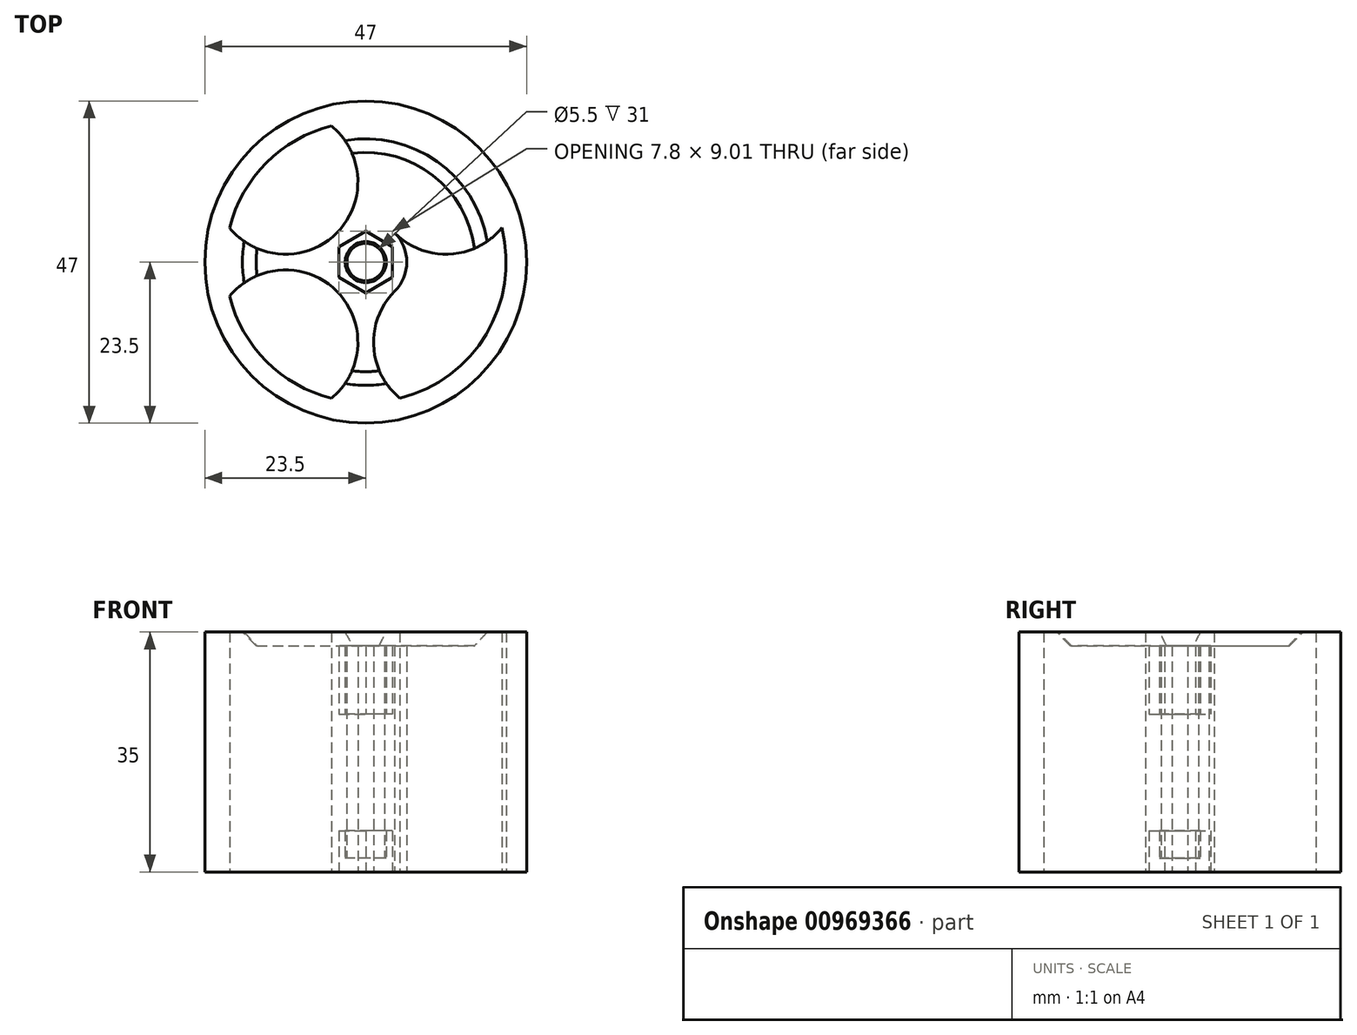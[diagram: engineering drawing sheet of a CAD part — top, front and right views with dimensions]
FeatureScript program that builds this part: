
annotation { "Feature Type Name" : "Feature", "Feature Type Description" : "" }
export const myFeature = defineFeature(function(context is Context, id is Id, definition is map)
    precondition{}
    {
        {
            var Q0;
            Q0=qCreatedBy(makeId("Top.planeOp"),FACE);
            var sketch = newSketch(context, id + "F0", { "sketchPlane" : qUnion([Q0])});
            skCircle(sketch, "E0", {"center": v(0, 0) * mm, "radius": 22.5 * mm});
            skCircle(sketch, "E1", {"center": v(0, 0) * mm, "radius": 20.5 * mm});
            skCircle(sketch, "E2", {"center": v(0, 0) * mm, "radius": 23.5 * mm});
            skCircle(sketch, "E3", {"center": v(0, 0) * mm, "radius": 6 * mm});
            skArc(sketch, "E4", {"start": v(-19.88, 5) * mm, "mid": v(-4.24, 4.24) * mm, "end": v(-5, 19.88) * mm});
            skArc(sketch, "E5.MirrorCS", {"start": v(19.88, 5) * mm, "mid": v(4.24, 4.24) * mm, "end": v(5, 19.88) * mm});
            skArc(sketch, "E6.MirrorCS", {"start": v(-19.88, -5) * mm, "mid": v(-4.24, -4.24) * mm, "end": v(-5, -19.88) * mm});
            skArc(sketch, "E7.MirrorCS", {"start": v(19.88, -5) * mm, "mid": v(4.24, -4.24) * mm, "end": v(5, -19.88) * mm});
            skCircle(sketch, "E8.cCircle", {"center": v(0, 0) * mm, "radius": 3.9 * mm, "construction": true});
            skLineSegment(sketch, "E8.0", {"start": v(-3.9, 2.25) * mm, "end": v(0, 4.5) * mm});
            skLineSegment(sketch, "E8.1", {"start": v(0, 4.5) * mm, "end": v(3.9, 2.25) * mm});
            skLineSegment(sketch, "E8.2", {"start": v(3.9, 2.25) * mm, "end": v(3.9, -2.25) * mm});
            skLineSegment(sketch, "E8.3", {"start": v(3.9, -2.25) * mm, "end": v(0, -4.5) * mm});
            skLineSegment(sketch, "E8.4", {"start": v(0, -4.5) * mm, "end": v(-3.9, -2.25) * mm});
            skLineSegment(sketch, "E8.5", {"start": v(-3.9, -2.25) * mm, "end": v(-3.9, 2.25) * mm});
            skPoint(sketch, "E8.0.midPoint", {"position": v(-1.95, 3.38) * mm});
            skCircle(sketch, "E9", {"center": v(0, 0) * mm, "radius": 2.75 * mm});
            skCircle(sketch, "E10", {"center": v(0, 0) * mm, "radius": 3 * mm});
            skSolve(sketch);
        }
        {
            var Q0;
            Q0=makeQuery(id+"F0.imprint","IMPRINT",FACE,{"disambiguationData":[TD([[makeQuery(id+"F0.imprint","IMPRINT",EDGE,{"derivedFrom":sQuery(id+"F0.wireOp",EDGE,"E0")}),1.0]])]});
            var Q1;
            Q1=makeQuery(id+"F0.imprint","IMPRINT",FACE,{"disambiguationData":[TD([[makeQuery(id+"F0.imprint","IMPRINT",EDGE,{"derivedFrom":sQuery(id+"F0.wireOp",EDGE,"E0")}),-1.0]])]});
            var Q2;
            {var subQ0=sQuery(id+"F0.wireOp",EDGE,"E4");var subQ1=sQuery(id+"F0.wireOp",EDGE,"E1");var subQ2=makeQuery(id+"F0.imprint","INTERSECT",VERTEX,{"disambiguationData":[OD(1.0)],"derivedFrom":[subQ1,subQ0]});Q2=makeQuery(id+"F0.imprint","IMPRINT",FACE,{"disambiguationData":[TD([[makeQuery(id+"F0.imprint","IMPRINT",EDGE,{"disambiguationData":[TD([[subQ2,1.0]])],"derivedFrom":subQ1}),1.0]])]});}
            var Q3;
            {var subQ0=sQuery(id+"F0.wireOp",EDGE,"E5.MirrorCS");var subQ1=sQuery(id+"F0.wireOp",EDGE,"E1");var subQ2=makeQuery(id+"F0.imprint","INTERSECT",VERTEX,{"disambiguationData":[OD(0.0)],"derivedFrom":[subQ1,subQ0]});Q3=makeQuery(id+"F0.imprint","IMPRINT",FACE,{"disambiguationData":[TD([[makeQuery(id+"F0.imprint","IMPRINT",EDGE,{"disambiguationData":[TD([[subQ2,1.0]])],"derivedFrom":subQ1}),1.0]])]});}
            var Q4;
            {var subQ0=sQuery(id+"F0.wireOp",EDGE,"E6.MirrorCS");var subQ1=sQuery(id+"F0.wireOp",EDGE,"E1");var subQ2=makeQuery(id+"F0.imprint","INTERSECT",VERTEX,{"disambiguationData":[OD(1.0)],"derivedFrom":[subQ1,subQ0]});Q4=makeQuery(id+"F0.imprint","IMPRINT",FACE,{"disambiguationData":[TD([[makeQuery(id+"F0.imprint","IMPRINT",EDGE,{"disambiguationData":[TD([[subQ2,-1.0]])],"derivedFrom":subQ1}),1.0]])]});}
            var Q5;
            {var subQ0=sQuery(id+"F0.wireOp",EDGE,"E4");var subQ1=sQuery(id+"F0.wireOp",EDGE,"E1");var subQ2=makeQuery(id+"F0.imprint","INTERSECT",VERTEX,{"disambiguationData":[OD(0.0)],"derivedFrom":[subQ1,subQ0]});Q5=makeQuery(id+"F0.imprint","IMPRINT",FACE,{"disambiguationData":[TD([[makeQuery(id+"F0.imprint","IMPRINT",EDGE,{"disambiguationData":[TD([[subQ2,-1.0]])],"derivedFrom":subQ1}),1.0]])]});}
            var Q6;
            Q6=makeQuery(id+"F0.imprint","IMPRINT",FACE,{"disambiguationData":[TD([[makeQuery(id+"F0.imprint","IMPRINT",EDGE,{"derivedFrom":sQuery(id+"F0.wireOp",EDGE,"E8.0")}),1.0]])]});
            var Q7;
            Q7=makeQuery(id+"F0.imprint","IMPRINT",FACE,{"disambiguationData":[TD([[makeQuery(id+"F0.imprint","IMPRINT",EDGE,{"derivedFrom":sQuery(id+"F0.wireOp",EDGE,"E8.0")}),-1.0]])]});
            extrude(context, id + "F1", {"entities" : qUnion([Q0, Q1, Q2, Q3, Q4, Q5, Q6, Q7]), "depth" : 35 * mm, "offsetDistance" : 25 * mm});
        }
        {
            var Q0;
            Q0=makeQuery(id+"F0.imprint","IMPRINT",FACE,{"disambiguationData":[TD([[makeQuery(id+"F0.imprint","IMPRINT",EDGE,{"derivedFrom":sQuery(id+"F0.wireOp",EDGE,"E9")}),-1.0]])]});
            extrude(context, id + "F2", {"entities" : qUnion([Q0]), "operationType" : NewBodyOperationType.ADD, "depth" : 33 * mm, "offsetDistance" : 25 * mm, "hasSecondDirection" : true, "secondDirectionOppositeDirection" : false, "secondDirectionDepth" : 2 * mm});
        }
        {
            var Q0;
            Q0=makeQuery(id+"F1.opExtrude","CAP_EDGE",EDGE,{"disambiguationData":[OSD([sQuery(id+"F0.wireOp",EDGE,"E10")])],"isStart":false});
            chamfer(context, id + "F3", {"entities" : qUnion([Q0]), "width" : 15 * mm, "tangentPropagation" : true});
        }
        {
            var Q0;
            Q0=makeQuery(id+"F0.imprint","IMPRINT",FACE,{"disambiguationData":[TD([[makeQuery(id+"F0.imprint","IMPRINT",EDGE,{"derivedFrom":sQuery(id+"F0.wireOp",EDGE,"E8.0")}),-1.0]])]});
            extrude(context, id + "F4", {"entities" : qUnion([Q0]), "operationType" : NewBodyOperationType.REMOVE, "depth" : 6 * mm, "offsetDistance" : 25 * mm});
        }
        {
            var Q0;
            Q0=makeQuery(id+"F0.imprint","IMPRINT",FACE,{"disambiguationData":[TD([[makeQuery(id+"F0.imprint","IMPRINT",EDGE,{"derivedFrom":sQuery(id+"F0.wireOp",EDGE,"E8.0")}),-1.0]])]});
            extrude(context, id + "F5", {"entities" : qUnion([Q0]), "operationType" : NewBodyOperationType.REMOVE, "depth" : 35 * mm, "offsetDistance" : 25 * mm, "hasSecondDirection" : true, "secondDirectionOppositeDirection" : false, "secondDirectionDepth" : 23 * mm});
        }
    });
